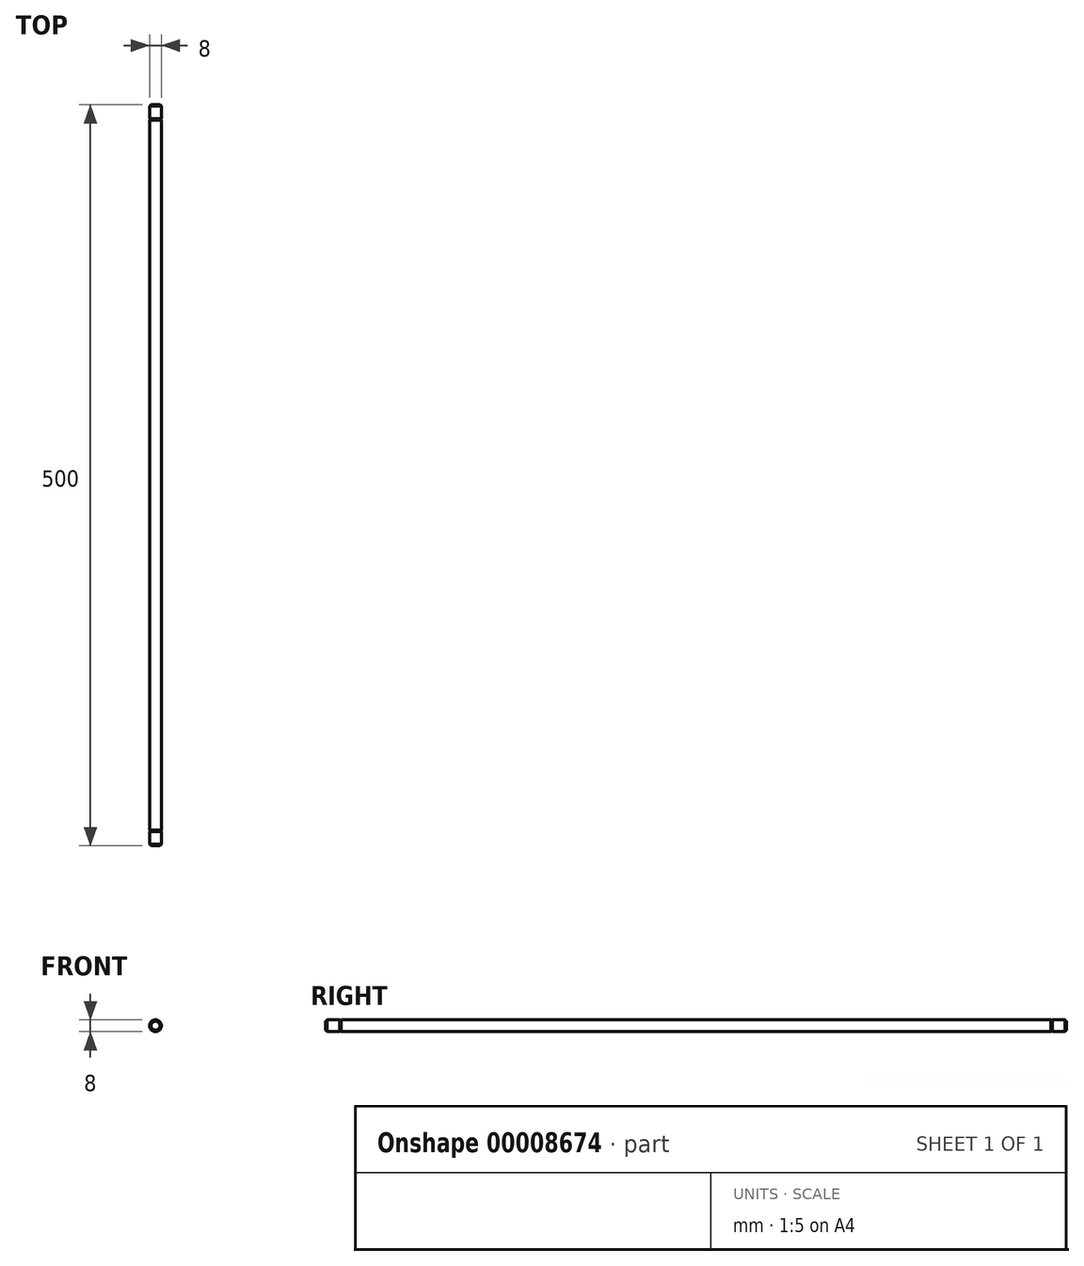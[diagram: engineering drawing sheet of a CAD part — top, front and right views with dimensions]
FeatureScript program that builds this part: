
annotation { "Feature Type Name" : "Feature", "Feature Type Description" : "" }
export const myFeature = defineFeature(function(context is Context, id is Id, definition is map)
    precondition{}
    {
        {
            var Q0;
            Q0=qCreatedBy(makeId("Top.planeOp"),FACE);
            var sketch = newSketch(context, id + "F0", { "sketchPlane" : qUnion([Q0])});
            skLineSegment(sketch, "E0.rect.bottom", {"start": v(4, -250) * mm, "end": v(-4, -250) * mm});
            skLineSegment(sketch, "E0.rect.top", {"start": v(4, 250) * mm, "end": v(-4, 250) * mm});
            skLineSegment(sketch, "E0.rect.left", {"start": v(4, -250) * mm, "end": v(4, 250) * mm});
            skLineSegment(sketch, "E0.rect.right", {"start": v(-4, -250) * mm, "end": v(-4, 250) * mm});
            skPoint(sketch, "E0.rect.middle", {"position": v(0, 0) * mm});
            skLineSegment(sketch, "E1", {"start": v(0, 250) * mm, "end": v(0, -250) * mm});
            skCircle(sketch, "E2", {"center": v(-4, 240) * mm, "radius": 0.5 * mm});
            skCircle(sketch, "E3", {"center": v(-4, -240) * mm, "radius": 0.5 * mm});
            skLineSegment(sketch, "E4", {"start": v(-4, 249) * mm, "end": v(-3, 250) * mm});
            skLineSegment(sketch, "E5", {"start": v(-4, -249) * mm, "end": v(-3, -250) * mm});
            skSolve(sketch);
        }
        {
            var Q0;
            {var subQ8=sQuery(id+"F0.wireOp",EDGE,"E1");Q0=makeQuery(id+"F0.imprint","IMPRINT",FACE,{"disambiguationData":[TD([[makeQuery(id+"F0.imprint","IMPRINT",EDGE,{"derivedFrom":subQ8}),-1.0]])]});}
            var Q1;
            Q1=sQuery(id+"F0.wireOp",EDGE,"E1");
            revolve(context, id + "F1", {"entities" : qUnion([Q0]), "axis" : qUnion([Q1]), "revolveType" : RevolveType.FULL});
        }
    });
